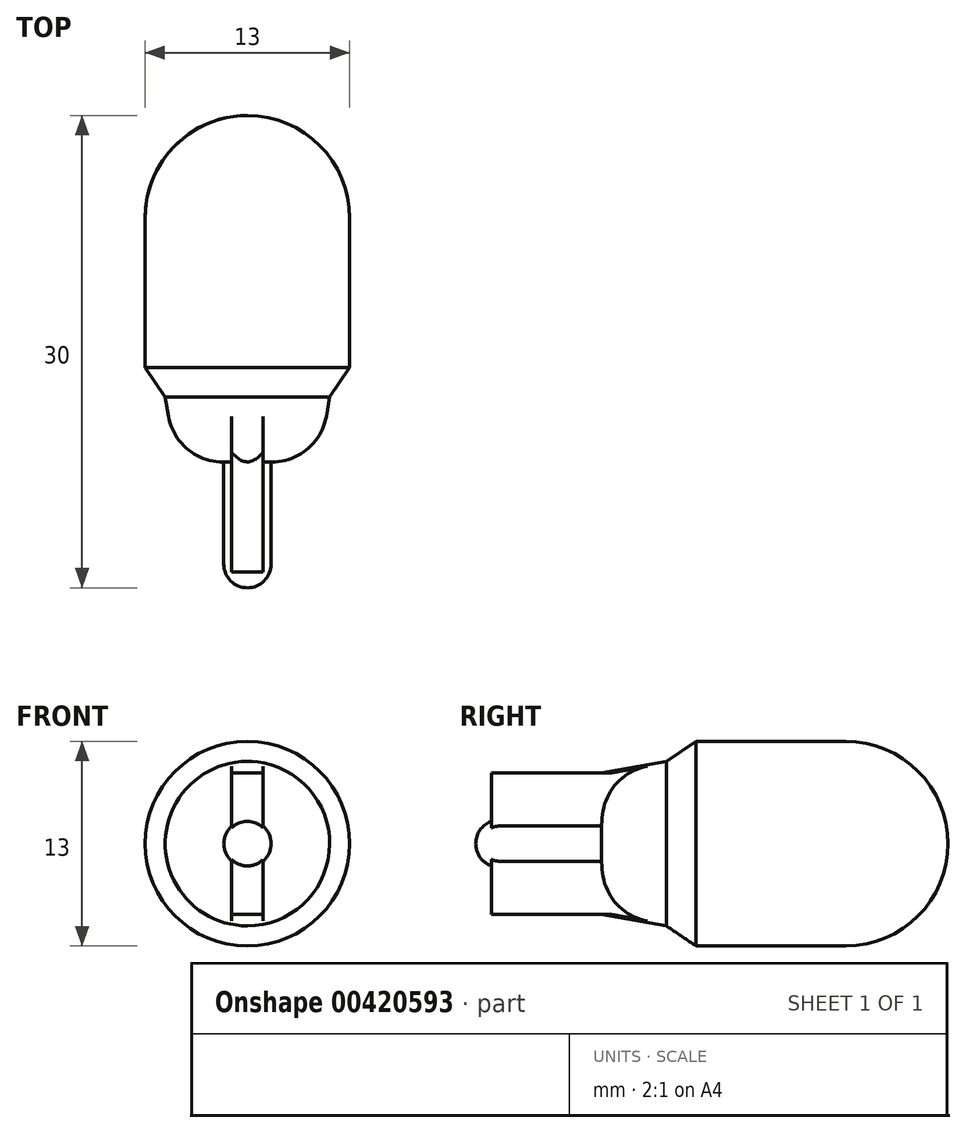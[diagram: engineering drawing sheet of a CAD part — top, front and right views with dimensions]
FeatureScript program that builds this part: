
annotation { "Feature Type Name" : "Feature", "Feature Type Description" : "" }
export const myFeature = defineFeature(function(context is Context, id is Id, definition is map)
    precondition{}
    {
        {
            var Q0;
            Q0=qCreatedBy(makeId("Top.planeOp"),FACE);
            var sketch = newSketch(context, id + "F0", { "sketchPlane" : qUnion([Q0])});
            skLineSegment(sketch, "E0", {"start": v(0, 0) * mm, "end": v(0, 22) * mm});
            skArc(sketch, "E1", {"start": v(0, 22) * mm, "mid": v(-4.6, 20.1) * mm, "end": v(-6.5, 15.5) * mm});
            skLineSegment(sketch, "E2", {"start": v(0, 22) * mm, "end": v(-10.43, 22) * mm, "construction": true});
            skLineSegment(sketch, "E3", {"start": v(-6.5, 15.5) * mm, "end": v(-6.5, 6) * mm});
            skLineSegment(sketch, "E4", {"start": v(-6.5, 6) * mm, "end": v(-5.22, 4.1) * mm});
            skLineSegment(sketch, "E5", {"start": v(-5.22, 4.1) * mm, "end": v(-4.5, 0) * mm});
            skLineSegment(sketch, "E6", {"start": v(-4.5, 0) * mm, "end": v(0, 0) * mm});
            skSolve(sketch);
        }
        {
            var Q0;
            Q0 = qSketchRegion(id + "F0", true);
            var Q1;
            Q1=sQuery(id+"F0.wireOp",EDGE,"E0");
            revolve(context, id + "F1", {"entities" : qUnion([Q0]), "axis" : qUnion([Q1]), "revolveType" : RevolveType.FULL});
        }
        {
            var Q0;
            Q0=makeQuery(id+"F1.opRevolve","SWEPT_FACE",FACE,{"disambiguationData":[OSD([sQuery(id+"F0.wireOp",EDGE,"E6")])]});
            var sketch = newSketch(context, id + "F2", { "sketchPlane" : qUnion([Q0])});
            skCircle(sketch, "E7", {"center": v(0, 0) * mm, "radius": 1.5 * mm});
            skSolve(sketch);
        }
        {
            var Q0;
            Q0 = qSketchRegion(id + "F2", true);
            extrude(context, id + "F3", {"entities" : qUnion([Q0]), "operationType" : NewBodyOperationType.ADD, "depth" : 8 * mm, "offsetDistance" : 25 * mm});
        }
        {
            var Q0;
            Q0=makeQuery(id+"F1.opRevolve","SWEPT_FACE",FACE,{"disambiguationData":[OSD([sQuery(id+"F0.wireOp",EDGE,"E6")])]});
            var sketch = newSketch(context, id + "F4", { "sketchPlane" : qUnion([Q0])});
            skLineSegment(sketch, "E8.bottom", {"start": v(-1, 4.5) * mm, "end": v(1, 4.5) * mm});
            skLineSegment(sketch, "E8.top", {"start": v(-1, -4.5) * mm, "end": v(1, -4.5) * mm});
            skLineSegment(sketch, "E8.left", {"start": v(-1, 4.5) * mm, "end": v(-1, -4.5) * mm});
            skLineSegment(sketch, "E8.right", {"start": v(1, 4.5) * mm, "end": v(1, -4.5) * mm});
            skPoint(sketch, "E8.middle", {"position": v(0, 0) * mm});
            skSolve(sketch);
        }
        {
            var Q0;
            Q0 = qSketchRegion(id + "F4", true);
            extrude(context, id + "F5", {"entities" : qUnion([Q0]), "operationType" : NewBodyOperationType.ADD, "depth" : 7 * mm, "offsetDistance" : 25 * mm, "hasSecondDirection" : true, "secondDirectionBound" : BoundingType.UP_TO_NEXT, "secondDirectionOppositeDirection" : true, "secondDirectionDepth" : 25 * mm});
        }
        {
            var Q0;
            {var subQ0=sQuery(id+"F0.wireOp",EDGE,"E5");var subQ1=sQuery(id+"F0.wireOp",EDGE,"E6");Q0=makeQuery(id+"F5.boolean.opBoolean","SPLIT",EDGE,{"disambiguationData":[TD([makeQuery(id+"F5.opExtrude","SWEPT_FACE",FACE,{"disambiguationData":[OSD([sQuery(id+"F4.wireOp",EDGE,"E8.left")])]})])],"derivedFrom":makeQuery(id+"F1.opRevolve","SWEPT_EDGE",EDGE,{"disambiguationData":[OSD([subQ0,subQ1])]})});}
            var Q1;
            {var subQ0=sQuery(id+"F0.wireOp",EDGE,"E5");var subQ1=sQuery(id+"F0.wireOp",EDGE,"E6");Q1=makeQuery(id+"F5.boolean.opBoolean","SPLIT",EDGE,{"disambiguationData":[TD([makeQuery(id+"F5.opExtrude","SWEPT_FACE",FACE,{"disambiguationData":[OSD([sQuery(id+"F4.wireOp",EDGE,"E8.right")])]})])],"derivedFrom":makeQuery(id+"F1.opRevolve","SWEPT_EDGE",EDGE,{"disambiguationData":[OSD([subQ0,subQ1])]})});}
            fillet(context, id + "F6", {"entities" : qUnion([Q0, Q1]), "radius" : 3.5 * mm, "tangentPropagation" : true, "allowEdgeOverflow" : false});
        }
        {
            var Q0;
            Q0=makeQuery(id+"F3.opExtrude","CAP_EDGE",EDGE,{"disambiguationData":[OSD([sQuery(id+"F2.wireOp",EDGE,"E7")])],"isStart":false});
            fillet(context, id + "F7", {"entities" : qUnion([Q0]), "radius" : 1.5 * mm, "tangentPropagation" : true, "allowEdgeOverflow" : false});
        }
    });
